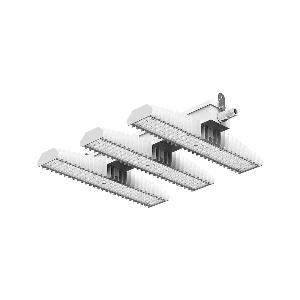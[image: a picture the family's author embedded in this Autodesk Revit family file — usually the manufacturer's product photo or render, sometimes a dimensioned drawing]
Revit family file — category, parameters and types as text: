
# Revit family: 3f_filippi_-_3f_lem_ampio_3f_filippi_-_58901_-_3f_lem_3_led_150_dali_cr_ampio
name_source: partatom
category: Lighting Fixtures
units: mm (PartAtom-declared; Revit-internal decimal feet)

## family parameters
Cut with Voids When Loaded = No
Host = Face
Light Source = No
Part Type = Normal
Room Calculation Point = No
Round Connector Dimension = Use Diameter
Shared = No

## types (1)
- 3F Filippi - 3F LEM Ampio (1 x LED, 25484 lm, 165 W, 4000 K)
    Apparent Load = 165 VA
    Approval mark = CE
    CIE Flux Codes = 60 92 99 100 100
    Color Rendering = 80
    Color Temperature = 4000 K
    Control Gear = Electronic transformer
    Default Elevation = 1800 mm
    Description = Industrial luminaire with high light output and high luminous efficiency designed with the most innovative technologies for environments with temperature up to 55°C.

ILLUMINOTECHNICAL
Luminous efficiency 100% (DLOR 100%, ULOR 0%).
Initial luminous flux of the luminaire 25484 lm.
Direct symmetric wide distribution: the illuminated area has a rectangular shape.
Installation Interdistance Transv.D = 1.58 x hu - Long.D = 1.45 x hu.
Tabular UGR (CIE 117 - 4H-8H; S=0.25H; 70/50/20): RUG 23.2 - 24.2.
Beam angle: 93° - 99°.
Luminous efficacy 154 lm/W.
Lifetime (L93/B10): 30000 h. (tq+25°C)
Lifetime (L90/B10): 50000 h. (tq+25°C)
Lifetime (L85/B10): 80000 h. (tq+25°C)
Lifetime (L80/B10): 100000 h. (tq+25°C)
Lifetime (L85/B10): 50000 h. (tq+55°C)
Sudden decreased luminous flux after 50000 hours: 0% (C0).
Photobiological safety in compliance with IEC/TR 62778: RG0 risk exempt, (IEC 62471).
In compliance with IEC/EN 62722-2-1 - IEC/EN 62717 standards.

SOURCE
3 Mid-Power linear LED modules 50W/840.
Energy efficiency class (UE 2019/2020 - UE 2019/2015): C.
CIE 13.3 Colour rendering index: CRI >80 (R9 <50%).
IES TM-30 Fidelity Index: Rf = 84 Rg = 95.
CCT nominal colour temperature 4000 K.
Colour initial tolerance (MacAdam): SDCM 3.

MECHANICAL
Passive modular heatsinks in die-casted aluminium, painted in white colour.
To optimize the thermal management of the LED module, the heatsinks are oversized and provided with self-cleaning of cooling fins.
Wiring body in aluminium and galvanised steel anchored solidly to the sinks and thermally separated.
3F Lens lenses with high luminous efficiency, transparent methacrylate (PMMA), fixed to the LED modules.
Fixing brackets in stainless steel.
Luminaire with limited surface temperature. - D - (EN 60598-2-24)
Dimensions: 657x542 mm, height 129 mm. Weight 13.685 kg.
IP65 protection degree.
Mechanical strength to impacts IK06 (1 joule).
Glow-wire test resistance 650°C.

ELECTRICAL
Halogen Free DALI-2 DATI (Parts 251, 252, 253), PUSH-DIM, electronic wiring 230V-50/60Hz, power factor 0.97 at full load, THD <25%, constant output current, class I, 2 driver, 2 DALI addresses.
Power of the luminaire 165 W.
ENEC - CE.
SAFE FLICKER: PstLM=<1 and SVM=<0.4 (IEC TR 61547-1 and IEC TR 63158), to ensure a more comfortable and safe light.
Luminaire compliant with EN 60598-2-22 for power supply from a centralised emergency system CPSS (Central Power Supply System), not incorporated in the luminaire - high risk areas excluded. The default power and flux are 100% in AC and 15% in DC.
Ambient temperature from -30°C to +55°C.
Temperature class T6 max 85°C.
Quick connection via M25 5P connector with 9-13 mm tightening range.
Power unit positioned on a separate compartment by the LED module to ensure optimum temperatures of cabling components, to be inspectable and maintainable.
Relative humidity UR: <85%.

INSTALLATION
Ceiling / Suspended / Wall.
All accessories dedicated to this product are available on the Catalog and on our website www.3F-Filippi.com.

APPLICATIONS
In commercial environments, exhibition and industrial areas, stores, open areas.
Applications with high ambient temperature up to 55°C.
Environments in which it is necessary a total protection against falling fragments (eg environments with foodstuffs or machines with moving parts or with extreme temperature changes), use luminaires with polycarbonate lenses.

LIGHT MANAGEMENT
Recommended minimum setting: 10%.
The luminaire, equipped with (DALI-2 DATI) driver, can be controlled manually with 3F Easy Dim technology or automatically/manually with wired or wireless DALI/D2D control systems.
The D2D driver guarantees interoperability with other devices with the same certification by making the following information available:
Device Data (Part 251), Energy Report (Part 252), Diagnosis & Maintenance (Part 253).
In electrical systems without a regulation system (manual or automatic) and DALI bus, a suitable jumper must be made on the DA-DA terminals of the appliance.

WARNING
Fixture not suitable for cold stores with an ambient temperature <0°C and/or relative humidity >85%.
Luminaire designed for disposal/recycling at end-of-life.
Replaceable (LED only) light source by a professional. Replaceable control gear by a professional.
    Height = 129 mm
    Lamp = 1 x LED
    Lamp Light Flux = 25484 lm
    Lamp Power = 165 W
    Lamp count = 1
    Length = 657 mm
    Lifetime = 50000 h
    Luminous efficacy = 154 lm/W
    Manufacturer = 3F Filippi
    ModVariant = No
    Model = 3F Filippi - 58901 - 3F LEM 3 LED 150 DALI CR AMPIO
    Mounting Place = Ceiling
    Mounting Type = Pendant
    Number of Poles = 1
    OnlyDefault = Yes
    Power Factor = 1
    Product Name = 3F Filippi - 3F LEM Ampio
    Product group = pendant luminaire
    ProductGroupID = 9
    Protection Class = Protection class I
    Protection Degree = IP 65
    RLX_Detail_Level = 1
    RLX_Emergency_Light_Flux = 0 lm
    RLX_Emergency_Type = 0
    RLX_Emergency_Type_DB = No
    RlxData = <blob elided: 102913 chars, md5=2d45e3be>
    Socket = socket
    Standby Power = 0 W
    System Light Flux = 25484 lm
    System Power = 165 W
    Type Comments = Product without accessories
    Type Image = 3f_filippi_-_lem_3.jpg
    URL = http://relux.com
    VarID = ---
    Voltage = 0 V
    Weight = 0.00 kg
    Width = 542 mm

## geometry (parser evidence)
native form markers: Blend x4, Sweep x12
no freeform markers — native parametric forms only
